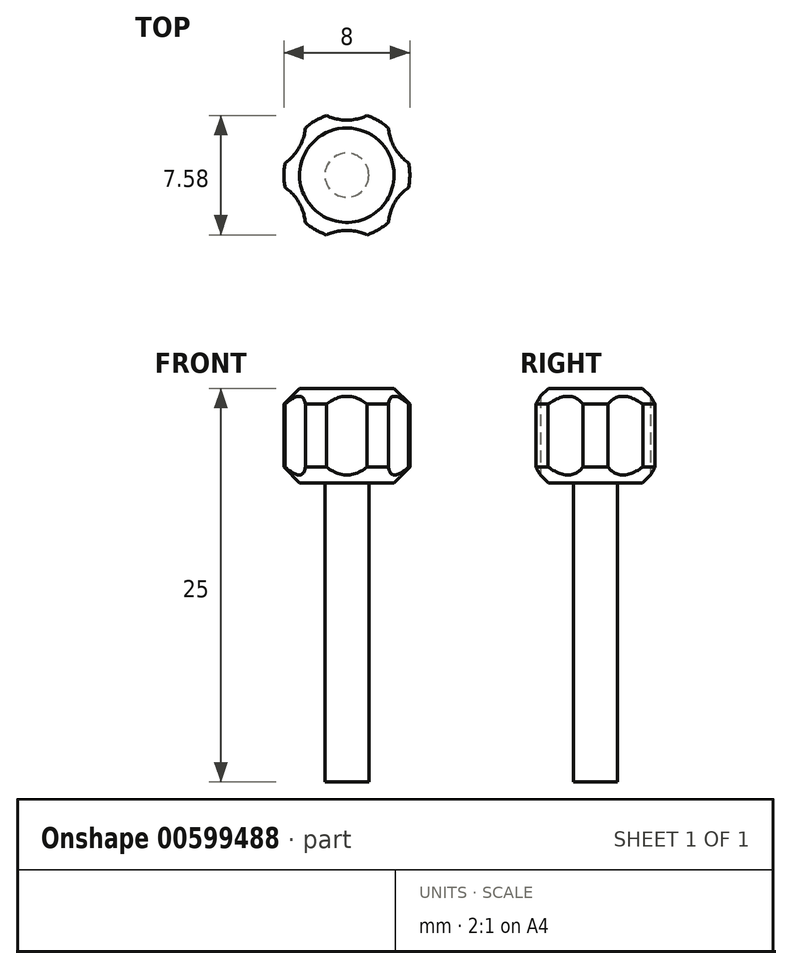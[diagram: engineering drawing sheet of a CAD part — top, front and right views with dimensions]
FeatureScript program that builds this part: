
annotation { "Feature Type Name" : "Feature", "Feature Type Description" : "" }
export const myFeature = defineFeature(function(context is Context, id is Id, definition is map)
    precondition{}
    {
        {
            var Q0;
            Q0=qCreatedBy(makeId("Top.planeOp"),FACE);
            var sketch = newSketch(context, id + "F0", { "sketchPlane" : qUnion([Q0])});
            skCircle(sketch, "E0", {"center": v(0, 0) * mm, "radius": 4 * mm});
            skCircle(sketch, "E1", {"center": v(0, 0) * mm, "radius": 1.4 * mm});
            skCircle(sketch, "E2", {"center": v(0, 6.5) * mm, "radius": 3 * mm});
            skCircle(sketch, "E3.1.0", {"center": v(-5.63, 3.25) * mm, "radius": 3 * mm});
            skCircle(sketch, "E3.2.0", {"center": v(-5.63, -3.25) * mm, "radius": 3 * mm});
            skCircle(sketch, "E3.3.0", {"center": v(0, -6.5) * mm, "radius": 3 * mm});
            skCircle(sketch, "E3.4.0", {"center": v(5.63, -3.25) * mm, "radius": 3 * mm});
            skCircle(sketch, "E3.5.0", {"center": v(5.63, 3.25) * mm, "radius": 3 * mm});
            skSolve(sketch);
        }
        {
            var Q0;
            Q0=makeQuery(id+"F0.imprint","IMPRINT",FACE,{"disambiguationData":[TD([[makeQuery(id+"F0.imprint","IMPRINT",EDGE,{"derivedFrom":sQuery(id+"F0.wireOp",EDGE,"E1")}),-1.0]])]});
            var Q1;
            Q1=makeQuery(id+"F0.imprint","IMPRINT",FACE,{"disambiguationData":[TD([[makeQuery(id+"F0.imprint","IMPRINT",EDGE,{"derivedFrom":sQuery(id+"F0.wireOp",EDGE,"E1")}),1.0]])]});
            var Q2;
            {var subQ0=sQuery(id+"F0.wireOp",EDGE,"E2");var subQ1=sQuery(id+"F0.wireOp",EDGE,"E0");var subQ2=makeQuery(id+"F0.imprint","INTERSECT",VERTEX,{"disambiguationData":[OD(0.0)],"derivedFrom":[subQ1,subQ0]});Q2=makeQuery(id+"F0.imprint","IMPRINT",FACE,{"disambiguationData":[TD([[makeQuery(id+"F0.imprint","IMPRINT",EDGE,{"disambiguationData":[TD([[subQ2,-1.0]])],"derivedFrom":subQ1}),1.0]])]});}
            var Q3;
            {var subQ0=sQuery(id+"F0.wireOp",EDGE,"E3.5.0");var subQ1=sQuery(id+"F0.wireOp",EDGE,"E0");var subQ2=makeQuery(id+"F0.imprint","INTERSECT",VERTEX,{"disambiguationData":[OD(0.0)],"derivedFrom":[subQ1,subQ0]});Q3=makeQuery(id+"F0.imprint","IMPRINT",FACE,{"disambiguationData":[TD([[makeQuery(id+"F0.imprint","IMPRINT",EDGE,{"disambiguationData":[TD([[subQ2,1.0]])],"derivedFrom":subQ1}),1.0]])]});}
            var Q4;
            {var subQ0=sQuery(id+"F0.wireOp",EDGE,"E3.4.0");var subQ1=sQuery(id+"F0.wireOp",EDGE,"E0");var subQ2=makeQuery(id+"F0.imprint","INTERSECT",VERTEX,{"disambiguationData":[OD(0.0)],"derivedFrom":[subQ1,subQ0]});Q4=makeQuery(id+"F0.imprint","IMPRINT",FACE,{"disambiguationData":[TD([[makeQuery(id+"F0.imprint","IMPRINT",EDGE,{"disambiguationData":[TD([[subQ2,-1.0]])],"derivedFrom":subQ1}),1.0]])]});}
            var Q5;
            {var subQ0=sQuery(id+"F0.wireOp",EDGE,"E3.3.0");var subQ1=sQuery(id+"F0.wireOp",EDGE,"E0");var subQ2=makeQuery(id+"F0.imprint","INTERSECT",VERTEX,{"disambiguationData":[OD(0.0)],"derivedFrom":[subQ1,subQ0]});Q5=makeQuery(id+"F0.imprint","IMPRINT",FACE,{"disambiguationData":[TD([[makeQuery(id+"F0.imprint","IMPRINT",EDGE,{"disambiguationData":[TD([[subQ2,-1.0]])],"derivedFrom":subQ1}),1.0]])]});}
            var Q6;
            {var subQ0=sQuery(id+"F0.wireOp",EDGE,"E3.2.0");var subQ1=sQuery(id+"F0.wireOp",EDGE,"E0");var subQ2=makeQuery(id+"F0.imprint","INTERSECT",VERTEX,{"disambiguationData":[OD(0.0)],"derivedFrom":[subQ1,subQ0]});Q6=makeQuery(id+"F0.imprint","IMPRINT",FACE,{"disambiguationData":[TD([[makeQuery(id+"F0.imprint","IMPRINT",EDGE,{"disambiguationData":[TD([[subQ2,-1.0]])],"derivedFrom":subQ1}),1.0]])]});}
            var Q7;
            {var subQ0=sQuery(id+"F0.wireOp",EDGE,"E3.1.0");var subQ1=sQuery(id+"F0.wireOp",EDGE,"E0");var subQ2=makeQuery(id+"F0.imprint","INTERSECT",VERTEX,{"disambiguationData":[OD(0.0)],"derivedFrom":[subQ1,subQ0]});Q7=makeQuery(id+"F0.imprint","IMPRINT",FACE,{"disambiguationData":[TD([[makeQuery(id+"F0.imprint","IMPRINT",EDGE,{"disambiguationData":[TD([[subQ2,-1.0]])],"derivedFrom":subQ1}),1.0]])]});}
            extrude(context, id + "F1", {"entities" : qUnion([Q0, Q1, Q2, Q3, Q4, Q5, Q6, Q7]), "depth" : 6 * mm});
        }
        {
            var Q0;
            Q0=makeQuery(id+"F1.opExtrude","CAP_EDGE",EDGE,{"disambiguationData":[OSD([sQuery(id+"F0.wireOp",EDGE,"E0")])],"isStart":false});
            var Q1;
            Q1=makeQuery(id+"F1.opExtrude","CAP_EDGE",EDGE,{"disambiguationData":[OSD([sQuery(id+"F0.wireOp",EDGE,"E0")])],"isStart":true});
            chamfer(context, id + "F2", {"entities" : qUnion([Q0, Q1]), "width" : 1 * mm, "tangentPropagation" : true});
        }
        {
            var Q0;
            {var subQ0=sQuery(id+"F0.wireOp",EDGE,"E3.3.0");var subQ1=sQuery(id+"F0.wireOp",EDGE,"E0");var subQ2=makeQuery(id+"F0.imprint","INTERSECT",VERTEX,{"disambiguationData":[OD(0.0)],"derivedFrom":[subQ1,subQ0]});Q0=makeQuery(id+"F0.imprint","IMPRINT",FACE,{"disambiguationData":[TD([[makeQuery(id+"F0.imprint","IMPRINT",EDGE,{"disambiguationData":[TD([[subQ2,-1.0]])],"derivedFrom":subQ1}),1.0]])]});}
            var Q1;
            {var subQ0=sQuery(id+"F0.wireOp",EDGE,"E3.2.0");var subQ1=sQuery(id+"F0.wireOp",EDGE,"E0");var subQ2=makeQuery(id+"F0.imprint","INTERSECT",VERTEX,{"disambiguationData":[OD(0.0)],"derivedFrom":[subQ1,subQ0]});Q1=makeQuery(id+"F0.imprint","IMPRINT",FACE,{"disambiguationData":[TD([[makeQuery(id+"F0.imprint","IMPRINT",EDGE,{"disambiguationData":[TD([[subQ2,-1.0]])],"derivedFrom":subQ1}),1.0]])]});}
            var Q2;
            {var subQ0=sQuery(id+"F0.wireOp",EDGE,"E3.4.0");var subQ1=sQuery(id+"F0.wireOp",EDGE,"E0");var subQ2=makeQuery(id+"F0.imprint","INTERSECT",VERTEX,{"disambiguationData":[OD(0.0)],"derivedFrom":[subQ1,subQ0]});Q2=makeQuery(id+"F0.imprint","IMPRINT",FACE,{"disambiguationData":[TD([[makeQuery(id+"F0.imprint","IMPRINT",EDGE,{"disambiguationData":[TD([[subQ2,-1.0]])],"derivedFrom":subQ1}),1.0]])]});}
            var Q3;
            {var subQ0=sQuery(id+"F0.wireOp",EDGE,"E3.5.0");var subQ1=sQuery(id+"F0.wireOp",EDGE,"E0");var subQ2=makeQuery(id+"F0.imprint","INTERSECT",VERTEX,{"disambiguationData":[OD(0.0)],"derivedFrom":[subQ1,subQ0]});Q3=makeQuery(id+"F0.imprint","IMPRINT",FACE,{"disambiguationData":[TD([[makeQuery(id+"F0.imprint","IMPRINT",EDGE,{"disambiguationData":[TD([[subQ2,1.0]])],"derivedFrom":subQ1}),1.0]])]});}
            var Q4;
            {var subQ0=sQuery(id+"F0.wireOp",EDGE,"E2");var subQ1=sQuery(id+"F0.wireOp",EDGE,"E0");var subQ2=makeQuery(id+"F0.imprint","INTERSECT",VERTEX,{"disambiguationData":[OD(0.0)],"derivedFrom":[subQ1,subQ0]});Q4=makeQuery(id+"F0.imprint","IMPRINT",FACE,{"disambiguationData":[TD([[makeQuery(id+"F0.imprint","IMPRINT",EDGE,{"disambiguationData":[TD([[subQ2,-1.0]])],"derivedFrom":subQ1}),1.0]])]});}
            var Q5;
            {var subQ0=sQuery(id+"F0.wireOp",EDGE,"E3.1.0");var subQ1=sQuery(id+"F0.wireOp",EDGE,"E0");var subQ2=makeQuery(id+"F0.imprint","INTERSECT",VERTEX,{"disambiguationData":[OD(0.0)],"derivedFrom":[subQ1,subQ0]});Q5=makeQuery(id+"F0.imprint","IMPRINT",FACE,{"disambiguationData":[TD([[makeQuery(id+"F0.imprint","IMPRINT",EDGE,{"disambiguationData":[TD([[subQ2,-1.0]])],"derivedFrom":subQ1}),1.0]])]});}
            extrude(context, id + "F3", {"entities" : qUnion([Q0, Q1, Q2, Q3, Q4, Q5]), "operationType" : NewBodyOperationType.REMOVE, "endBound" : BoundingType.THROUGH_ALL, "depth" : 25 * mm});
        }
        {
            var Q0;
            Q0=makeQuery(id+"F0.imprint","IMPRINT",FACE,{"disambiguationData":[TD([[makeQuery(id+"F0.imprint","IMPRINT",EDGE,{"derivedFrom":sQuery(id+"F0.wireOp",EDGE,"E1")}),1.0]])]});
            extrude(context, id + "F4", {"entities" : qUnion([Q0]), "operationType" : NewBodyOperationType.ADD, "oppositeDirection" : true, "depth" : 19 * mm, "offsetDistance" : 25 * mm});
        }
    });
